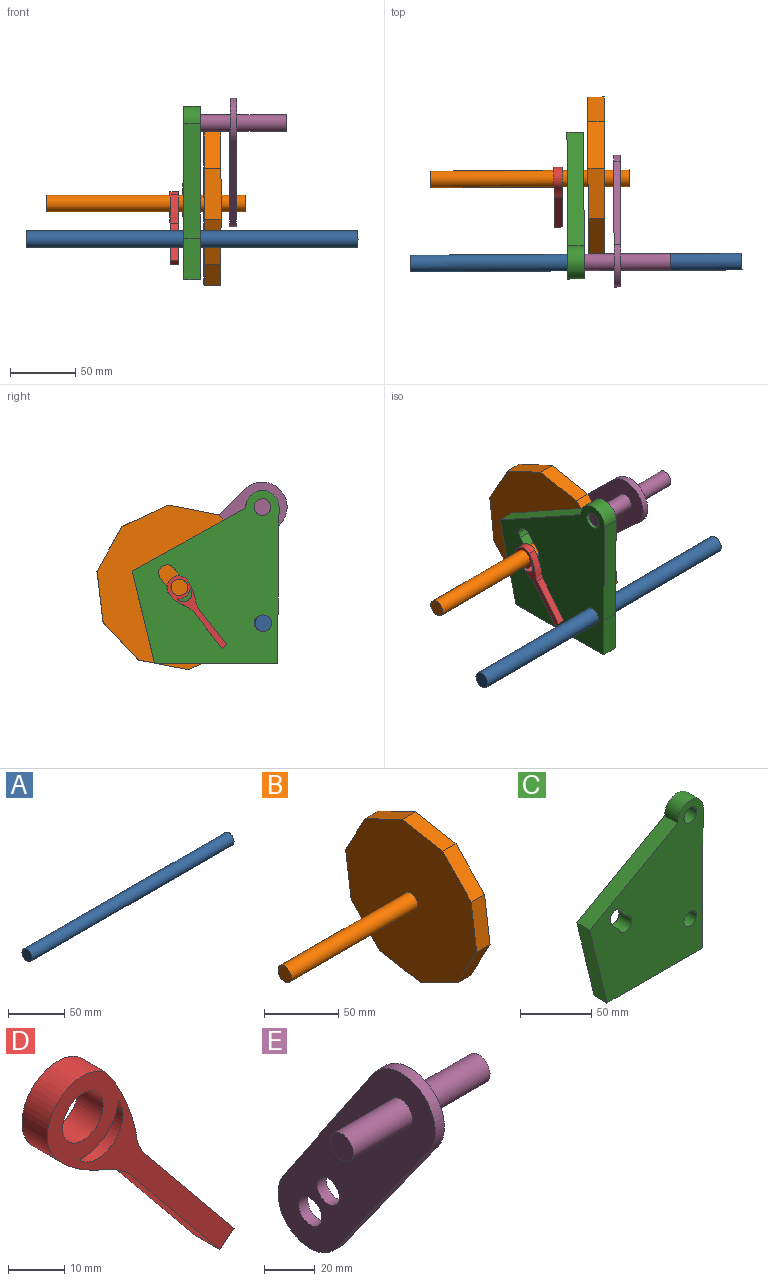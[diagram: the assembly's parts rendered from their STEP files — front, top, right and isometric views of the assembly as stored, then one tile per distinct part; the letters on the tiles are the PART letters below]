
ASSEMBLY  parts=5 mates=4
PART A: 3 faces, bbox 254x12.7x12.7 mm
  f0: cylinder r=6.35mm len=254mm, axis (-1,0,0), area 10134.1mm2, adj f1,f2
  f1: plane 12.7x12.7mm, normal (1,0,0), area 126.7mm2, adj f0
  f2: plane 12.7x12.7mm, normal (-1,0,0), area 126.7mm2, adj f0
PART B: 16 faces, bbox 152.4x125x125.8 mm
  f0: plane 35.35x17.04mm, normal (0,-0.43,-0.9), area 498.4mm2, adj f1,f9,f10,f11
  f1: plane 38.62x12.7mm, normal (0,0.18,-0.98), area 498.4mm2, adj f0,f2,f10,f11
  f2: plane 28.36x27.13mm, normal (0,0.72,-0.69), area 498.4mm2, adj f1,f3,f10,f11
  f3: plane 38.89x12.7mm, normal (0,0.99,-0.13), area 498.4mm2, adj f2,f4,f10,f11
  f4: plane 34.57x18.58mm, normal (0,0.88,0.47), area 498.4mm2, adj f3,f5,f10,f11
  f5: plane 35.35x17.04mm, normal (0,0.43,0.9), area 498.4mm2, adj f4,f6,f10,f11
  f6: plane 38.62x12.7mm, normal (0,-0.18,0.98), area 498.4mm2, adj f5,f7,f10,f11
  f7: plane 28.36x27.13mm, normal (0,-0.72,0.69), area 498.4mm2, adj f6,f8,f10,f11
  f8: plane 38.89x12.7mm, normal (0,-0.99,0.13), area 498.4mm2, adj f7,f9,f10,f11
  f9: plane 34.57x18.58mm, normal (0,-0.88,-0.47), area 498.4mm2, adj f0,f8,f10,f11
  f10: plane 125.84x124.97mm, normal (1,0,0), area 11723.8mm2, adj f0,f1,f2,f3,f4,f5,f6,f7
  f11: plane 125.84x124.97mm, normal (-1,0,0), area 11723.8mm2, adj f0,f1,f2,f3,f4,f5,f6,f7
  f12: cylinder r=6.35mm len=19.05mm, axis (-1,0,0), area 760.1mm2, adj f10,f13
  f13: plane 12.7x12.7mm, normal (1,0,0), area 126.7mm2, adj f12
  f14: cylinder r=6.35mm len=120.65mm, axis (1,0,0), area 4813.7mm2, adj f11,f15
  f15: plane 12.7x12.7mm, normal (-1,0,0), area 126.7mm2, adj f14
PART C: 14 faces, bbox 112.3x12.7x132.6 mm
  f0: plane 12.7x10.89mm, normal (-0.77,0,-0.63), area 178.4mm2, adj f1,f8,f12,f13
  f1: cylinder r=6.35mm len=12.7mm, axis (0,1,0), area 253.4mm2, adj f0,f2,f12,f13
  f2: plane 12.7x10.89mm, normal (0.77,0,0.63), area 178.4mm2, adj f1,f8,f12,f13
  f3: plane 87.98x12.7mm, normal (1,0,-0.01), area 1117.4mm2, adj f4,f9,f12,f13
  f4: cylinder r=12.7mm len=25.4mm, axis (0,1,0), area 517.2mm2, adj f3,f5,f12,f13
  f5: plane 86.96x48.22mm, normal (-0.48,0,0.87), area 1262.8mm2, adj f4,f6,f12,f13
  f6: plane 70.97x17.14mm, normal (-0.97,0,-0.23), area 927.2mm2, adj f5,f7,f12,f13
  f7: plane 94.32x12.7mm, normal (0,0,-1), area 1197.9mm2, adj f6,f9,f12,f13
  f8: cylinder r=6.35mm len=12.7mm, axis (0,1,0), area 253.4mm2, adj f0,f2,f12,f13
  f9: plane 31.78x12.7mm, normal (1,0,0), area 403.6mm2, adj f3,f7,f12,f13
  f10: cylinder r=6.35mm len=12.7mm, axis (0,1,0), area 506.7mm2, adj f12,f13
  f11: cylinder r=6.35mm len=12.7mm, axis (0,1,0), area 506.7mm2, adj f12,f13
  f12: plane 132.59x112.34mm, normal (0,-1,0), area 10331.3mm2, adj f0,f1,f2,f3,f4,f5,f6,f7
  f13: plane 132.59x112.34mm, normal (0,1,0), area 10331.3mm2, adj f0,f1,f2,f3,f4,f5,f6,f7
PART D: 11 faces, bbox 46.7x6.4x54.8 mm
  f0: cylinder r=8.89mm len=9.82mm, axis (0,1,0), area 89.6mm2, adj f6,f9,f10
  f1: plane 28.29x23.11mm, normal (0.77,0,0.63), area 232mm2, adj f2,f7,f9,f10
  f2: extruded ~21.57x9.05mm, area 150mm2, adj f1,f3,f9,f10
  f3: cylinder r=8.89mm len=15.36mm, axis (0,1,0), area 173.8mm2, adj f2,f4,f9,f10
  f4: extruded ~17.28x11.16mm, area 131.5mm2, adj f3,f5,f9,f10
  f5: plane 28.29x23.11mm, normal (-0.77,0,-0.63), area 232mm2, adj f4,f7,f9,f10
  f6: cylinder r=6.35mm len=11.03mm, axis (0,1,0), area 122mm2, adj f0,f9,f10
  f7: plane 6.35x3.55mm, normal (0.63,0,-0.77), area 29.1mm2, adj f1,f5,f9,f10
  f8: cylinder r=5.08mm len=10.17mm, axis (0,1,0), area 202.8mm2, adj f9,f10
  f9: plane 54.8x46.73mm, normal (0,-1,0), area 428.2mm2, adj f0,f1,f2,f3,f4,f5,f6,f7
  f10: plane 54.8x46.73mm, normal (0,1,0), area 428.2mm2, adj f0,f1,f2,f3,f4,f5,f6,f7
PART E: 12 faces, bbox 76.2x87.6x110 mm
  f0: cylinder r=17.89mm len=32.96mm, axis (1,0,0), area 287.7mm2, adj f1,f4,f6,f7
  f1: plane 73.49x49.58mm, normal (0,0.83,0.56), area 450.4mm2, adj f0,f2,f6,f7
  f2: cylinder r=19.05mm len=34.97mm, axis (1,0,0), area 318.1mm2, adj f1,f4,f6,f7
  f3: cylinder r=6.17mm len=12.34mm, axis (1,0,0), area 196.9mm2, adj f6,f7
  f4: plane 70.01x49.84mm, normal (0,-0.81,-0.58), area 436.6mm2, adj f0,f2,f6,f7
  f5: cylinder r=6.38mm len=12.76mm, axis (1,0,0), area 203.6mm2, adj f6,f7
  f6: plane 109.98x87.62mm, normal (-1,0,0), area 3976.7mm2, adj f0,f1,f2,f3,f4,f5,f10
  f7: plane 109.98x87.62mm, normal (1,0,0), area 3976.7mm2, adj f0,f1,f2,f3,f4,f5,f9
  f8: plane 12.7x12.7mm, normal (1,0,0), area 126.7mm2, adj f9
  f9: cylinder r=6.35mm len=38.1mm, axis (-1,0,0), area 1520.1mm2, adj f7,f8
  f10: cylinder r=6.35mm len=33.02mm, axis (-1,0,0), area 1317.4mm2, adj f6,f11
  f11: plane 12.7x12.7mm, normal (-1,0,0), area 126.7mm2, adj f10
PLACE A rot(axis=(-0.78,0,0.63),0.5deg) t=(-202.88,-35.6,-85.85)mm
PLACE B rot(axis=(-1,0,0),179.1deg) t=(-187.65,77.57,-17.62)mm
PLACE C rot(axis=(0,0,-1),89.7deg) t=(-196.53,-35.57,-85.85)mm fixed
PLACE D rot(axis=(0.01,0.01,-1),89.7deg) t=(-213.22,-3.75,-57.89)mm
PLACE E rot(axis=(1,0,0.03),11.5deg) t=(-175.17,4.83,-31.32)mm
MATE revolute C.f4 <-> E.f2  axis (1,0.01,0) through (-202.88,-35.6,3.05)mm
MATE revolute B.f12 <-> D.f0  axis (1,0.01,0) through (-254.04,28.33,-58.42)mm
MATE revolute E.f0 <-> B.f12  axis (1,0.01,0) through (-171.49,28.8,-58.42)mm
MATE revolute A.f0 <-> C.f10  axis (-1,-0.01,0) through (-202.88,-35.6,-85.85)mm
